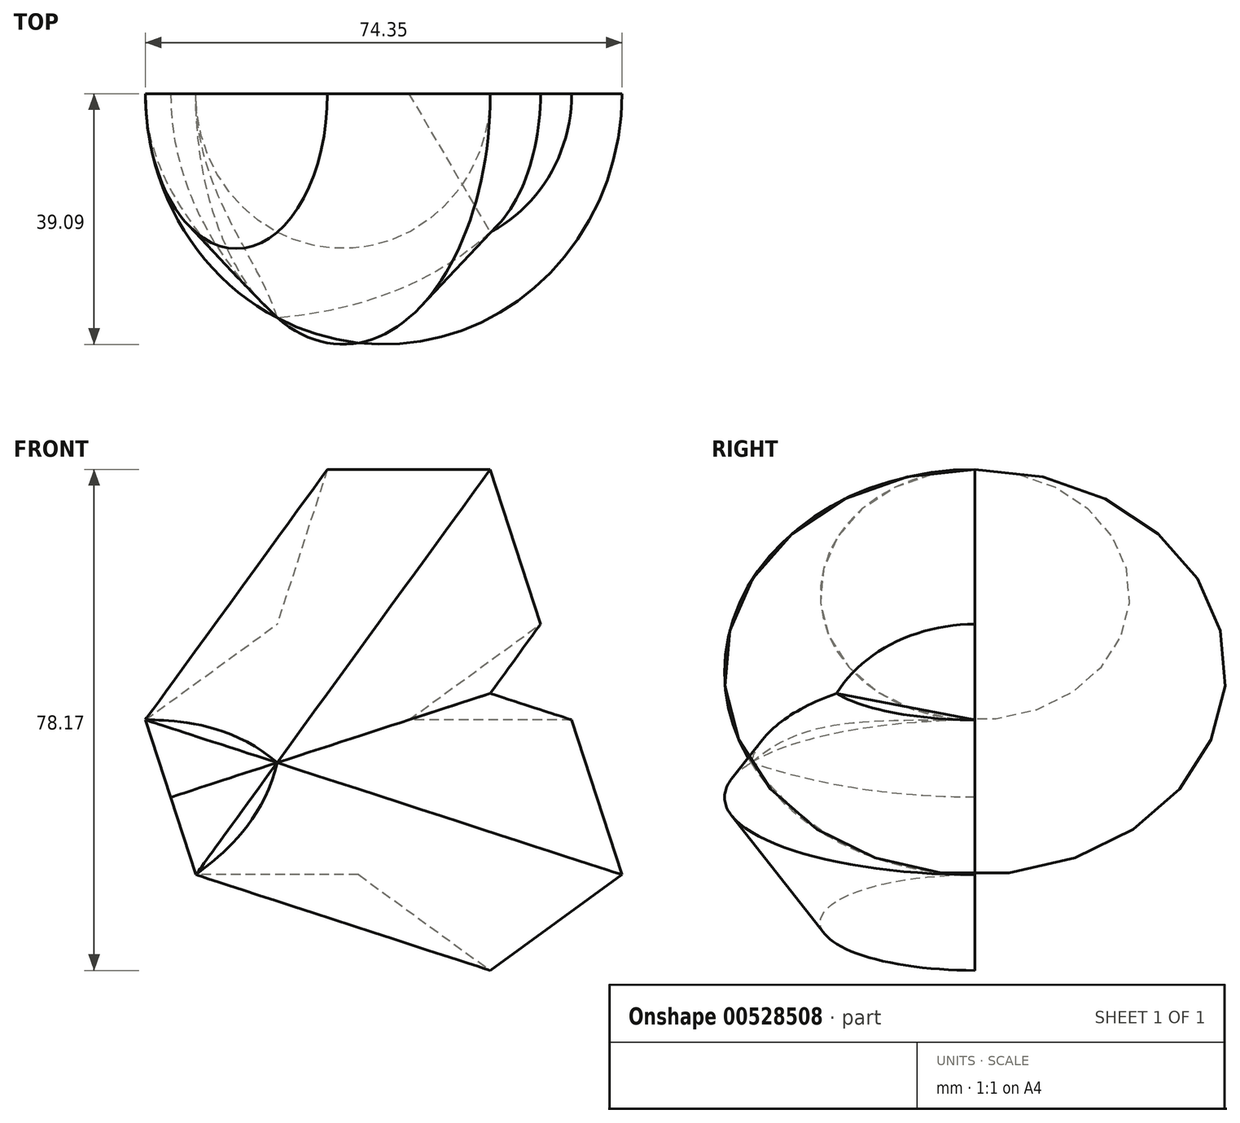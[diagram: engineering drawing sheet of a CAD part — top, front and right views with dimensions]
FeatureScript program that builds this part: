
annotation { "Feature Type Name" : "Feature", "Feature Type Description" : "" }
export const myFeature = defineFeature(function(context is Context, id is Id, definition is map)
    precondition{}
    {
        {
            var Q0;
            Q0=qCreatedBy(makeId("Front.planeOp"),FACE);
            var sketch = newSketch(context, id + "F0", { "sketchPlane" : qUnion([Q0])});
            skCircle(sketch, "E0.cCircle", {"center": v(0, 0) * mm, "radius": 17.48 * mm, "construction": true});
            skLineSegment(sketch, "E0.0", {"start": v(12.7, -17.48) * mm, "end": v(-12.7, -17.48) * mm});
            skLineSegment(sketch, "E0.1", {"start": v(-12.7, -17.48) * mm, "end": v(-20.55, 6.68) * mm});
            skLineSegment(sketch, "E0.2", {"start": v(-20.55, 6.68) * mm, "end": v(0, 21.6) * mm});
            skLineSegment(sketch, "E0.3", {"start": v(0, 21.6) * mm, "end": v(20.55, 6.68) * mm});
            skLineSegment(sketch, "E0.4", {"start": v(20.55, 6.68) * mm, "end": v(12.7, -17.48) * mm});
            skPoint(sketch, "E0.0.midPoint", {"position": v(0, -17.48) * mm});
            skSolve(sketch);
        }
        {
            var Q0;
            Q0=makeQuery(id+"F0.imprint","IMPRINT",FACE,{"disambiguationData":[TD([[makeQuery(id+"F0.imprint","IMPRINT",EDGE,{"derivedFrom":sQuery(id+"F0.wireOp",EDGE,"E0.0")}),-1.0]])]});
            var Q1;
            Q1=sQuery(id+"F0.wireOp",EDGE,"E0.3");
            revolve(context, id + "F1", {"entities" : qUnion([Q0]), "axis" : qUnion([Q1]), "revolveType" : RevolveType.ONE_DIRECTION, "oppositeDirection" : true, "angle" : 180 * degree});
        }
        {
            var Q0;
            Q0 = qSketchRegion(id + "F0", true);
            var Q1;
            Q1=sQuery(id+"F0.wireOp",EDGE,"E0.4");
            revolve(context, id + "F2", {"operationType" : NewBodyOperationType.ADD, "entities" : qUnion([Q0]), "axis" : qUnion([Q1]), "revolveType" : RevolveType.ONE_DIRECTION, "oppositeDirection" : true, "angle" : 180 * degree});
        }
    });
